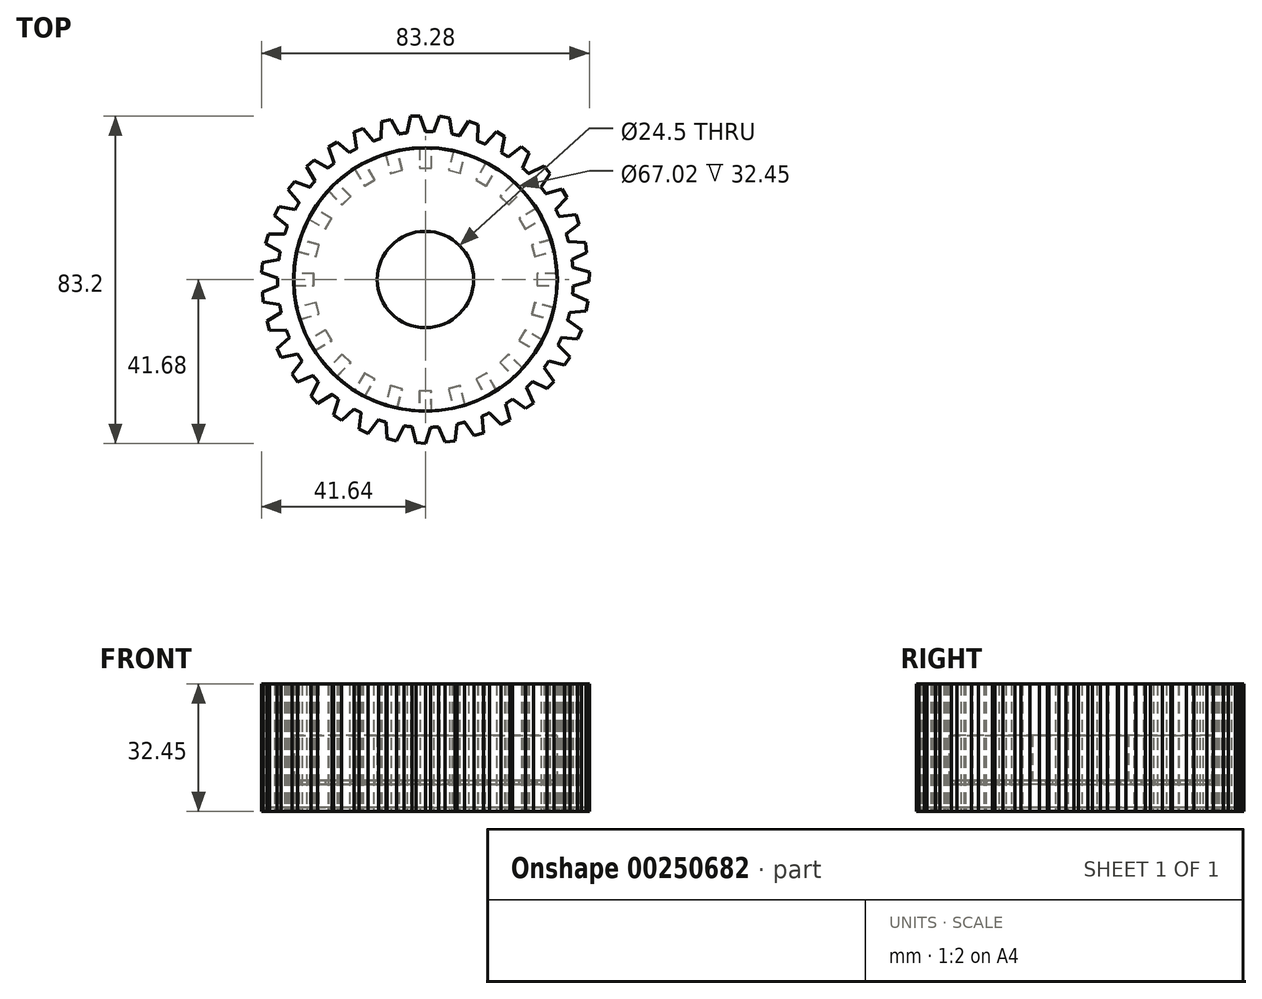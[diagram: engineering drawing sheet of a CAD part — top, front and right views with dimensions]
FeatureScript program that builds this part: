
annotation { "Feature Type Name" : "Feature", "Feature Type Description" : "" }
export const myFeature = defineFeature(function(context is Context, id is Id, definition is map)
    precondition{}
    {
        {
            var Q0;
            Q0=qCreatedBy(makeId("Top.planeOp"),FACE);
            var sketch = newSketch(context, id + "F0", { "sketchPlane" : qUnion([Q0])});
            skCircle(sketch, "E0", {"center": v(0, 0) * mm, "radius": 10.36 * mm});
            skCircle(sketch, "E1", {"center": v(0, 0) * mm, "radius": 33.51 * mm});
            skArc(sketch, "E2", {"start": v(-11.27, 35.85) * mm, "mid": v(-12.24, 35.53) * mm, "end": v(-13.2, 35.18) * mm});
            skLineSegment(sketch, "E3", {"start": v(-4.68, 37.29) * mm, "end": v(-3.82, 41.5) * mm});
            skLineSegment(sketch, "E4", {"start": v(-3.82, 41.5) * mm, "end": v(-1.33, 41.5) * mm});
            skLineSegment(sketch, "E5", {"start": v(-1.33, 41.5) * mm, "end": v(0, 37.58) * mm});
            skLineSegment(sketch, "E6.1.0", {"start": v(-11.27, 35.85) * mm, "end": v(-11.17, 40.16) * mm});
            skLineSegment(sketch, "E6.1.1", {"start": v(-11.17, 40.16) * mm, "end": v(-8.72, 40.6) * mm});
            skLineSegment(sketch, "E6.1.2", {"start": v(-8.72, 40.6) * mm, "end": v(-6.7, 36.97) * mm});
            skLineSegment(sketch, "E6.2.0", {"start": v(-17.49, 33.26) * mm, "end": v(-18.17, 37.52) * mm});
            skLineSegment(sketch, "E6.2.1", {"start": v(-18.17, 37.52) * mm, "end": v(-15.83, 38.4) * mm});
            skLineSegment(sketch, "E6.2.2", {"start": v(-15.83, 38.4) * mm, "end": v(-13.2, 35.18) * mm});
            skLineSegment(sketch, "E6.3.0", {"start": v(-23.14, 29.6) * mm, "end": v(-24.57, 33.67) * mm});
            skLineSegment(sketch, "E6.3.1", {"start": v(-24.57, 33.67) * mm, "end": v(-22.43, 34.95) * mm});
            skLineSegment(sketch, "E6.3.2", {"start": v(-22.43, 34.95) * mm, "end": v(-19.27, 32.26) * mm});
            skLineSegment(sketch, "E6.4.0", {"start": v(-28.06, 25) * mm, "end": v(-30.19, 28.74) * mm});
            skLineSegment(sketch, "E6.4.1", {"start": v(-30.19, 28.74) * mm, "end": v(-28.31, 30.38) * mm});
            skLineSegment(sketch, "E6.4.2", {"start": v(-28.31, 30.38) * mm, "end": v(-24.72, 28.3) * mm});
            skLineSegment(sketch, "E6.5.0", {"start": v(-32.07, 19.59) * mm, "end": v(-34.84, 22.89) * mm});
            skLineSegment(sketch, "E6.5.1", {"start": v(-34.84, 22.89) * mm, "end": v(-33.28, 24.84) * mm});
            skLineSegment(sketch, "E6.5.2", {"start": v(-33.28, 24.84) * mm, "end": v(-29.38, 23.43) * mm});
            skLineSegment(sketch, "E6.6.0", {"start": v(-35.05, 13.54) * mm, "end": v(-38.36, 16.3) * mm});
            skLineSegment(sketch, "E6.6.1", {"start": v(-38.36, 16.3) * mm, "end": v(-37.18, 18.5) * mm});
            skLineSegment(sketch, "E6.6.2", {"start": v(-37.18, 18.5) * mm, "end": v(-33.1, 17.8) * mm});
            skLineSegment(sketch, "E6.7.0", {"start": v(-36.9, 7.07) * mm, "end": v(-40.66, 9.19) * mm});
            skLineSegment(sketch, "E6.7.1", {"start": v(-40.66, 9.19) * mm, "end": v(-39.89, 11.56) * mm});
            skLineSegment(sketch, "E6.7.2", {"start": v(-39.89, 11.56) * mm, "end": v(-35.74, 11.61) * mm});
            skLineSegment(sketch, "E6.8.0", {"start": v(-37.58, 0.36) * mm, "end": v(-41.64, 1.78) * mm});
            skLineSegment(sketch, "E6.8.1", {"start": v(-41.64, 1.78) * mm, "end": v(-41.3, 4.25) * mm});
            skLineSegment(sketch, "E6.8.2", {"start": v(-41.3, 4.25) * mm, "end": v(-37.24, 5.04) * mm});
            skLineSegment(sketch, "E6.9.0", {"start": v(-37.04, -6.35) * mm, "end": v(-41.3, -5.68) * mm});
            skLineSegment(sketch, "E6.9.1", {"start": v(-41.3, -5.68) * mm, "end": v(-41.4, -3.2) * mm});
            skLineSegment(sketch, "E6.9.2", {"start": v(-41.4, -3.2) * mm, "end": v(-37.54, -1.69) * mm});
            skLineSegment(sketch, "E6.10.0", {"start": v(-35.3, -12.86) * mm, "end": v(-39.62, -12.97) * mm});
            skLineSegment(sketch, "E6.10.1", {"start": v(-39.62, -12.97) * mm, "end": v(-40.17, -10.53) * mm});
            skLineSegment(sketch, "E6.10.2", {"start": v(-40.17, -10.53) * mm, "end": v(-36.64, -8.36) * mm});
            skLineSegment(sketch, "E6.11.0", {"start": v(-32.44, -18.96) * mm, "end": v(-36.66, -19.83) * mm});
            skLineSegment(sketch, "E6.11.1", {"start": v(-36.66, -19.83) * mm, "end": v(-37.64, -17.54) * mm});
            skLineSegment(sketch, "E6.11.2", {"start": v(-37.64, -17.54) * mm, "end": v(-34.55, -14.77) * mm});
            skLineSegment(sketch, "E6.12.0", {"start": v(-28.54, -24.45) * mm, "end": v(-32.53, -26.06) * mm});
            skLineSegment(sketch, "E6.12.1", {"start": v(-32.53, -26.06) * mm, "end": v(-33.9, -23.98) * mm});
            skLineSegment(sketch, "E6.12.2", {"start": v(-33.9, -23.98) * mm, "end": v(-31.36, -20.7) * mm});
            skLineSegment(sketch, "E6.13.0", {"start": v(-23.71, -29.15) * mm, "end": v(-27.36, -31.45) * mm});
            skLineSegment(sketch, "E6.13.1", {"start": v(-27.36, -31.45) * mm, "end": v(-29.08, -29.64) * mm});
            skLineSegment(sketch, "E6.13.2", {"start": v(-29.08, -29.64) * mm, "end": v(-27.16, -25.97) * mm});
            skLineSegment(sketch, "E6.14.0", {"start": v(-18.13, -32.92) * mm, "end": v(-21.3, -35.83) * mm});
            skLineSegment(sketch, "E6.14.1", {"start": v(-21.3, -35.83) * mm, "end": v(-23.32, -34.36) * mm});
            skLineSegment(sketch, "E6.14.2", {"start": v(-23.32, -34.36) * mm, "end": v(-22.09, -30.4) * mm});
            skLineSegment(sketch, "E6.15.0", {"start": v(-11.96, -35.63) * mm, "end": v(-14.56, -39.06) * mm});
            skLineSegment(sketch, "E6.15.1", {"start": v(-14.56, -39.06) * mm, "end": v(-16.81, -37.97) * mm});
            skLineSegment(sketch, "E6.15.2", {"start": v(-16.81, -37.97) * mm, "end": v(-16.3, -33.86) * mm});
            skLineSegment(sketch, "E6.16.0", {"start": v(-5.4, -37.19) * mm, "end": v(-7.36, -41.03) * mm});
            skLineSegment(sketch, "E6.16.1", {"start": v(-7.36, -41.03) * mm, "end": v(-9.76, -40.36) * mm});
            skLineSegment(sketch, "E6.16.2", {"start": v(-9.76, -40.36) * mm, "end": v(-10, -36.22) * mm});
            skLineSegment(sketch, "E6.17.0", {"start": v(1.32, -37.56) * mm, "end": v(0.09, -41.68) * mm});
            skLineSegment(sketch, "E6.17.1", {"start": v(0.09, -41.68) * mm, "end": v(-2.4, -41.46) * mm});
            skLineSegment(sketch, "E6.17.2", {"start": v(-2.4, -41.46) * mm, "end": v(-3.37, -37.43) * mm});
            skLineSegment(sketch, "E6.18.0", {"start": v(8, -36.72) * mm, "end": v(7.53, -41) * mm});
            skLineSegment(sketch, "E6.18.1", {"start": v(7.53, -41) * mm, "end": v(5.04, -41.22) * mm});
            skLineSegment(sketch, "E6.18.2", {"start": v(5.04, -41.22) * mm, "end": v(3.37, -37.43) * mm});
            skLineSegment(sketch, "E6.19.0", {"start": v(14.43, -34.7) * mm, "end": v(14.73, -39) * mm});
            skLineSegment(sketch, "E6.19.1", {"start": v(14.73, -39) * mm, "end": v(12.32, -39.66) * mm});
            skLineSegment(sketch, "E6.19.2", {"start": v(12.32, -39.66) * mm, "end": v(10, -36.22) * mm});
            skLineSegment(sketch, "E6.20.0", {"start": v(20.4, -31.56) * mm, "end": v(21.46, -35.74) * mm});
            skLineSegment(sketch, "E6.20.1", {"start": v(21.46, -35.74) * mm, "end": v(19.2, -36.82) * mm});
            skLineSegment(sketch, "E6.20.2", {"start": v(19.2, -36.82) * mm, "end": v(16.3, -33.86) * mm});
            skLineSegment(sketch, "E6.21.0", {"start": v(25.7, -27.41) * mm, "end": v(27.5, -31.33) * mm});
            skLineSegment(sketch, "E6.21.1", {"start": v(27.5, -31.33) * mm, "end": v(25.47, -32.8) * mm});
            skLineSegment(sketch, "E6.21.2", {"start": v(25.47, -32.8) * mm, "end": v(22.09, -30.4) * mm});
            skLineSegment(sketch, "E6.22.0", {"start": v(30.19, -22.38) * mm, "end": v(32.64, -25.92) * mm});
            skLineSegment(sketch, "E6.22.1", {"start": v(32.64, -25.92) * mm, "end": v(30.92, -27.72) * mm});
            skLineSegment(sketch, "E6.22.2", {"start": v(30.92, -27.72) * mm, "end": v(27.16, -25.97) * mm});
            skLineSegment(sketch, "E6.23.0", {"start": v(33.7, -16.63) * mm, "end": v(36.75, -19.67) * mm});
            skLineSegment(sketch, "E6.23.1", {"start": v(36.75, -19.67) * mm, "end": v(35.37, -21.76) * mm});
            skLineSegment(sketch, "E6.23.2", {"start": v(35.37, -21.76) * mm, "end": v(31.36, -20.7) * mm});
            skLineSegment(sketch, "E6.24.0", {"start": v(36.13, -10.35) * mm, "end": v(39.67, -12.8) * mm});
            skLineSegment(sketch, "E6.24.1", {"start": v(39.67, -12.8) * mm, "end": v(38.69, -15.1) * mm});
            skLineSegment(sketch, "E6.24.2", {"start": v(38.69, -15.1) * mm, "end": v(34.55, -14.77) * mm});
            skLineSegment(sketch, "E6.25.0", {"start": v(37.4, -3.73) * mm, "end": v(41.32, -5.5) * mm});
            skLineSegment(sketch, "E6.25.1", {"start": v(41.32, -5.5) * mm, "end": v(40.76, -7.94) * mm});
            skLineSegment(sketch, "E6.25.2", {"start": v(40.76, -7.94) * mm, "end": v(36.64, -8.36) * mm});
            skLineSegment(sketch, "E6.26.0", {"start": v(37.46, 3) * mm, "end": v(41.64, 1.96) * mm});
            skLineSegment(sketch, "E6.26.1", {"start": v(41.64, 1.96) * mm, "end": v(41.53, -0.53) * mm});
            skLineSegment(sketch, "E6.26.2", {"start": v(41.53, -0.53) * mm, "end": v(37.54, -1.69) * mm});
            skLineSegment(sketch, "E6.27.0", {"start": v(36.32, 9.65) * mm, "end": v(40.62, 9.36) * mm});
            skLineSegment(sketch, "E6.27.1", {"start": v(40.62, 9.36) * mm, "end": v(40.95, 6.89) * mm});
            skLineSegment(sketch, "E6.27.2", {"start": v(40.95, 6.89) * mm, "end": v(37.24, 5.04) * mm});
            skLineSegment(sketch, "E6.28.0", {"start": v(34.01, 15.98) * mm, "end": v(38.3, 16.46) * mm});
            skLineSegment(sketch, "E6.28.1", {"start": v(38.3, 16.46) * mm, "end": v(39.06, 14.1) * mm});
            skLineSegment(sketch, "E6.28.2", {"start": v(39.06, 14.1) * mm, "end": v(35.74, 11.61) * mm});
            skLineSegment(sketch, "E6.29.0", {"start": v(30.61, 21.8) * mm, "end": v(34.74, 23.04) * mm});
            skLineSegment(sketch, "E6.29.1", {"start": v(34.74, 23.04) * mm, "end": v(35.92, 20.84) * mm});
            skLineSegment(sketch, "E6.29.2", {"start": v(35.92, 20.84) * mm, "end": v(33.1, 17.8) * mm});
            skLineSegment(sketch, "E6.30.0", {"start": v(26.23, 26.9) * mm, "end": v(30.07, 28.87) * mm});
            skLineSegment(sketch, "E6.30.1", {"start": v(30.07, 28.87) * mm, "end": v(31.62, 26.92) * mm});
            skLineSegment(sketch, "E6.30.2", {"start": v(31.62, 26.92) * mm, "end": v(29.38, 23.43) * mm});
            skLineSegment(sketch, "E6.31.0", {"start": v(21, 31.16) * mm, "end": v(24.43, 33.77) * mm});
            skLineSegment(sketch, "E6.31.1", {"start": v(24.43, 33.77) * mm, "end": v(26.3, 32.13) * mm});
            skLineSegment(sketch, "E6.31.2", {"start": v(26.3, 32.13) * mm, "end": v(24.72, 28.3) * mm});
            skLineSegment(sketch, "E6.32.0", {"start": v(15.1, 34.4) * mm, "end": v(18, 37.6) * mm});
            skLineSegment(sketch, "E6.32.1", {"start": v(18, 37.6) * mm, "end": v(20.15, 36.31) * mm});
            skLineSegment(sketch, "E6.32.2", {"start": v(20.15, 36.31) * mm, "end": v(19.27, 32.26) * mm});
            skLineSegment(sketch, "E6.33.0", {"start": v(8.72, 36.55) * mm, "end": v(11, 40.2) * mm});
            skLineSegment(sketch, "E6.33.1", {"start": v(11, 40.2) * mm, "end": v(13.34, 39.33) * mm});
            skLineSegment(sketch, "E6.33.2", {"start": v(13.34, 39.33) * mm, "end": v(13.2, 35.18) * mm});
            skLineSegment(sketch, "E6.34.0", {"start": v(2.05, 37.52) * mm, "end": v(3.65, 41.52) * mm});
            skLineSegment(sketch, "E6.34.1", {"start": v(3.65, 41.52) * mm, "end": v(6.1, 41.08) * mm});
            skLineSegment(sketch, "E6.34.2", {"start": v(6.1, 41.08) * mm, "end": v(6.7, 36.97) * mm});
            skArc(sketch, "E7.trimOffspring", {"start": v(-4.68, 37.29) * mm, "mid": v(-5.7, 37.14) * mm, "end": v(-6.7, 36.97) * mm});
            skArc(sketch, "E8.trimOffspring", {"start": v(2.05, 37.52) * mm, "mid": v(1.03, 37.56) * mm, "end": v(0, 37.58) * mm});
            skArc(sketch, "E9.trimOffspring", {"start": v(8.72, 36.55) * mm, "mid": v(7.72, 36.78) * mm, "end": v(6.7, 36.97) * mm});
            skArc(sketch, "E10.trimOffspring", {"start": v(15.1, 34.4) * mm, "mid": v(14.16, 34.8) * mm, "end": v(13.2, 35.18) * mm});
            skArc(sketch, "E11.trimOffspring", {"start": v(21, 31.16) * mm, "mid": v(20.15, 31.72) * mm, "end": v(19.27, 32.26) * mm});
            skArc(sketch, "E12.trimOffspring", {"start": v(26.23, 26.9) * mm, "mid": v(25.49, 27.61) * mm, "end": v(24.72, 28.3) * mm});
            skArc(sketch, "E13.trimOffspring", {"start": v(30.61, 21.8) * mm, "mid": v(30, 22.62) * mm, "end": v(29.38, 23.43) * mm});
            skArc(sketch, "E14.trimOffspring", {"start": v(34.01, 15.98) * mm, "mid": v(33.57, 16.9) * mm, "end": v(33.1, 17.8) * mm});
            skArc(sketch, "E15.trimOffspring", {"start": v(36.32, 9.65) * mm, "mid": v(36.04, 10.63) * mm, "end": v(35.74, 11.61) * mm});
            skArc(sketch, "E16.trimOffspring", {"start": v(37.46, 3) * mm, "mid": v(37.36, 4.03) * mm, "end": v(37.24, 5.04) * mm});
            skArc(sketch, "E17.trimOffspring", {"start": v(37.4, -3.73) * mm, "mid": v(37.48, -2.7) * mm, "end": v(37.54, -1.69) * mm});
            skArc(sketch, "E18.trimOffspring", {"start": v(36.13, -10.35) * mm, "mid": v(36.4, -9.36) * mm, "end": v(36.64, -8.36) * mm});
            skArc(sketch, "E19.trimOffspring", {"start": v(33.7, -16.63) * mm, "mid": v(34.14, -15.7) * mm, "end": v(34.55, -14.77) * mm});
            skArc(sketch, "E20.trimOffspring", {"start": v(30.19, -22.38) * mm, "mid": v(30.79, -21.55) * mm, "end": v(31.36, -20.7) * mm});
            skArc(sketch, "E21.trimOffspring", {"start": v(25.7, -27.41) * mm, "mid": v(26.44, -26.7) * mm, "end": v(27.16, -25.97) * mm});
            skArc(sketch, "E22.trimOffspring", {"start": v(20.4, -31.56) * mm, "mid": v(21.25, -31) * mm, "end": v(22.09, -30.4) * mm});
            skArc(sketch, "E23.trimOffspring", {"start": v(14.43, -34.7) * mm, "mid": v(15.37, -34.29) * mm, "end": v(16.3, -33.86) * mm});
            skArc(sketch, "E24.trimOffspring", {"start": v(8, -36.72) * mm, "mid": v(9, -36.48) * mm, "end": v(10, -36.22) * mm});
            skArc(sketch, "E25.trimOffspring", {"start": v(1.32, -37.56) * mm, "mid": v(2.35, -37.5) * mm, "end": v(3.37, -37.43) * mm});
            skArc(sketch, "E26.trimOffspring", {"start": v(-5.4, -37.19) * mm, "mid": v(-4.39, -37.32) * mm, "end": v(-3.37, -37.43) * mm});
            skArc(sketch, "E27.trimOffspring", {"start": v(-11.96, -35.63) * mm, "mid": v(-10.98, -35.94) * mm, "end": v(-10, -36.22) * mm});
            skArc(sketch, "E28.trimOffspring", {"start": v(-18.13, -32.92) * mm, "mid": v(-17.22, -33.4) * mm, "end": v(-16.3, -33.86) * mm});
            skArc(sketch, "E29.trimOffspring", {"start": v(-23.71, -29.15) * mm, "mid": v(-22.9, -29.79) * mm, "end": v(-22.09, -30.4) * mm});
            skArc(sketch, "E30.trimOffspring", {"start": v(-28.54, -24.45) * mm, "mid": v(-27.86, -25.22) * mm, "end": v(-27.16, -25.97) * mm});
            skArc(sketch, "E31.trimOffspring", {"start": v(-32.44, -18.96) * mm, "mid": v(-31.92, -19.84) * mm, "end": v(-31.36, -20.7) * mm});
            skArc(sketch, "E32.trimOffspring", {"start": v(-35.3, -12.86) * mm, "mid": v(-34.94, -13.82) * mm, "end": v(-34.55, -14.77) * mm});
            skArc(sketch, "E33.trimOffspring", {"start": v(-37.04, -6.35) * mm, "mid": v(-36.85, -7.36) * mm, "end": v(-36.64, -8.36) * mm});
            skArc(sketch, "E34.trimOffspring", {"start": v(-37.58, 0.36) * mm, "mid": v(-37.57, -0.66) * mm, "end": v(-37.54, -1.69) * mm});
            skArc(sketch, "E35.trimOffspring", {"start": v(-36.9, 7.07) * mm, "mid": v(-37.09, 6.06) * mm, "end": v(-37.24, 5.04) * mm});
            skArc(sketch, "E36.trimOffspring", {"start": v(-35.05, 13.54) * mm, "mid": v(-35.4, 12.58) * mm, "end": v(-35.74, 11.61) * mm});
            skArc(sketch, "E37.trimOffspring", {"start": v(-32.07, 19.59) * mm, "mid": v(-32.6, 18.7) * mm, "end": v(-33.1, 17.8) * mm});
            skArc(sketch, "E38.trimOffspring", {"start": v(-28.06, 25) * mm, "mid": v(-28.73, 24.22) * mm, "end": v(-29.38, 23.43) * mm});
            skArc(sketch, "E39.trimOffspring", {"start": v(-23.14, 29.6) * mm, "mid": v(-23.94, 28.96) * mm, "end": v(-24.72, 28.3) * mm});
            skArc(sketch, "E40.trimOffspring", {"start": v(-17.49, 33.26) * mm, "mid": v(-18.39, 32.77) * mm, "end": v(-19.27, 32.26) * mm});
            skSolve(sketch);
        }
        {
            var Q0;
            Q0 = qSketchRegion(id + "F0", true);
            extrude(context, id + "F1", {"entities" : qUnion([Q0]), "endBound" : BoundingType.SYMMETRIC, "depth" : 26.2 * mm});
        }
        {
            var Q0;
            Q0=qCreatedBy(makeId("Top.planeOp"),FACE);
            var sketch = newSketch(context, id + "F2", { "sketchPlane" : qUnion([Q0])});
            skCircle(sketch, "E41", {"center": v(0, 0) * mm, "radius": 33.42 * mm});
            skCircle(sketch, "E42", {"center": v(0, 0) * mm, "radius": 12.25 * mm});
            skSolve(sketch);
        }
        {
            var Q0;
            Q0 = qSketchRegion(id + "F2", true);
            var Q1;
            Q1=makeQuery(id+"F1.opExtrude","CAP_FACE",FACE,{"disambiguationData":[OSD([sQuery(id+"F0.wireOp",EDGE,"E1"),sQuery(id+"F0.wireOp",EDGE,"E2"),sQuery(id+"F0.wireOp",EDGE,"E3"),sQuery(id+"F0.wireOp",EDGE,"E4"),sQuery(id+"F0.wireOp",EDGE,"E5"),sQuery(id+"F0.wireOp",EDGE,"E6.1.0"),sQuery(id+"F0.wireOp",EDGE,"E6.1.1"),sQuery(id+"F0.wireOp",EDGE,"E6.1.2"),sQuery(id+"F0.wireOp",EDGE,"E6.2.0"),sQuery(id+"F0.wireOp",EDGE,"E6.2.1"),sQuery(id+"F0.wireOp",EDGE,"E6.2.2"),sQuery(id+"F0.wireOp",EDGE,"E6.3.0"),sQuery(id+"F0.wireOp",EDGE,"E6.3.1"),sQuery(id+"F0.wireOp",EDGE,"E6.3.2"),sQuery(id+"F0.wireOp",EDGE,"E6.4.0"),sQuery(id+"F0.wireOp",EDGE,"E6.4.1"),sQuery(id+"F0.wireOp",EDGE,"E6.4.2"),sQuery(id+"F0.wireOp",EDGE,"E6.5.0"),sQuery(id+"F0.wireOp",EDGE,"E6.5.1"),sQuery(id+"F0.wireOp",EDGE,"E6.5.2"),sQuery(id+"F0.wireOp",EDGE,"E6.6.0"),sQuery(id+"F0.wireOp",EDGE,"E6.6.1"),sQuery(id+"F0.wireOp",EDGE,"E6.6.2"),sQuery(id+"F0.wireOp",EDGE,"E6.7.0"),sQuery(id+"F0.wireOp",EDGE,"E6.7.1"),sQuery(id+"F0.wireOp",EDGE,"E6.7.2"),sQuery(id+"F0.wireOp",EDGE,"E6.8.0"),sQuery(id+"F0.wireOp",EDGE,"E6.8.1"),sQuery(id+"F0.wireOp",EDGE,"E6.8.2"),sQuery(id+"F0.wireOp",EDGE,"E6.9.0"),sQuery(id+"F0.wireOp",EDGE,"E6.9.1"),sQuery(id+"F0.wireOp",EDGE,"E6.9.2"),sQuery(id+"F0.wireOp",EDGE,"E6.10.0"),sQuery(id+"F0.wireOp",EDGE,"E6.10.1"),sQuery(id+"F0.wireOp",EDGE,"E6.10.2"),sQuery(id+"F0.wireOp",EDGE,"E6.11.0"),sQuery(id+"F0.wireOp",EDGE,"E6.11.1"),sQuery(id+"F0.wireOp",EDGE,"E6.11.2"),sQuery(id+"F0.wireOp",EDGE,"E6.12.0"),sQuery(id+"F0.wireOp",EDGE,"E6.12.1"),sQuery(id+"F0.wireOp",EDGE,"E6.12.2"),sQuery(id+"F0.wireOp",EDGE,"E6.13.0"),sQuery(id+"F0.wireOp",EDGE,"E6.13.1"),sQuery(id+"F0.wireOp",EDGE,"E6.13.2"),sQuery(id+"F0.wireOp",EDGE,"E6.14.0"),sQuery(id+"F0.wireOp",EDGE,"E6.14.1"),sQuery(id+"F0.wireOp",EDGE,"E6.14.2"),sQuery(id+"F0.wireOp",EDGE,"E6.15.0"),sQuery(id+"F0.wireOp",EDGE,"E6.15.1"),sQuery(id+"F0.wireOp",EDGE,"E6.15.2"),sQuery(id+"F0.wireOp",EDGE,"E6.16.0"),sQuery(id+"F0.wireOp",EDGE,"E6.16.1"),sQuery(id+"F0.wireOp",EDGE,"E6.16.2"),sQuery(id+"F0.wireOp",EDGE,"E6.17.0"),sQuery(id+"F0.wireOp",EDGE,"E6.17.1"),sQuery(id+"F0.wireOp",EDGE,"E6.17.2"),sQuery(id+"F0.wireOp",EDGE,"E6.18.0"),sQuery(id+"F0.wireOp",EDGE,"E6.18.1"),sQuery(id+"F0.wireOp",EDGE,"E6.18.2"),sQuery(id+"F0.wireOp",EDGE,"E6.19.0"),sQuery(id+"F0.wireOp",EDGE,"E6.19.1"),sQuery(id+"F0.wireOp",EDGE,"E6.19.2"),sQuery(id+"F0.wireOp",EDGE,"E6.20.0"),sQuery(id+"F0.wireOp",EDGE,"E6.20.1"),sQuery(id+"F0.wireOp",EDGE,"E6.20.2"),sQuery(id+"F0.wireOp",EDGE,"E6.21.0"),sQuery(id+"F0.wireOp",EDGE,"E6.21.1"),sQuery(id+"F0.wireOp",EDGE,"E6.21.2"),sQuery(id+"F0.wireOp",EDGE,"E6.22.0"),sQuery(id+"F0.wireOp",EDGE,"E6.22.1"),sQuery(id+"F0.wireOp",EDGE,"E6.22.2"),sQuery(id+"F0.wireOp",EDGE,"E6.23.0"),sQuery(id+"F0.wireOp",EDGE,"E6.23.1"),sQuery(id+"F0.wireOp",EDGE,"E6.23.2"),sQuery(id+"F0.wireOp",EDGE,"E6.24.0"),sQuery(id+"F0.wireOp",EDGE,"E6.24.1"),sQuery(id+"F0.wireOp",EDGE,"E6.24.2"),sQuery(id+"F0.wireOp",EDGE,"E6.25.0"),sQuery(id+"F0.wireOp",EDGE,"E6.25.1"),sQuery(id+"F0.wireOp",EDGE,"E6.25.2"),sQuery(id+"F0.wireOp",EDGE,"E6.26.0"),sQuery(id+"F0.wireOp",EDGE,"E6.26.1"),sQuery(id+"F0.wireOp",EDGE,"E6.26.2"),sQuery(id+"F0.wireOp",EDGE,"E6.27.0"),sQuery(id+"F0.wireOp",EDGE,"E6.27.1"),sQuery(id+"F0.wireOp",EDGE,"E6.27.2"),sQuery(id+"F0.wireOp",EDGE,"E6.28.0"),sQuery(id+"F0.wireOp",EDGE,"E6.28.1"),sQuery(id+"F0.wireOp",EDGE,"E6.28.2"),sQuery(id+"F0.wireOp",EDGE,"E6.29.0"),sQuery(id+"F0.wireOp",EDGE,"E6.29.1"),sQuery(id+"F0.wireOp",EDGE,"E6.29.2"),sQuery(id+"F0.wireOp",EDGE,"E6.30.0"),sQuery(id+"F0.wireOp",EDGE,"E6.30.1"),sQuery(id+"F0.wireOp",EDGE,"E6.30.2"),sQuery(id+"F0.wireOp",EDGE,"E6.31.0"),sQuery(id+"F0.wireOp",EDGE,"E6.31.1"),sQuery(id+"F0.wireOp",EDGE,"E6.31.2"),sQuery(id+"F0.wireOp",EDGE,"E6.32.0"),sQuery(id+"F0.wireOp",EDGE,"E6.32.1"),sQuery(id+"F0.wireOp",EDGE,"E6.32.2"),sQuery(id+"F0.wireOp",EDGE,"E6.33.0"),sQuery(id+"F0.wireOp",EDGE,"E6.33.1"),sQuery(id+"F0.wireOp",EDGE,"E6.33.2"),sQuery(id+"F0.wireOp",EDGE,"E6.34.0"),sQuery(id+"F0.wireOp",EDGE,"E6.34.1"),sQuery(id+"F0.wireOp",EDGE,"E6.34.2"),sQuery(id+"F0.wireOp",EDGE,"E7.trimOffspring"),sQuery(id+"F0.wireOp",EDGE,"E8.trimOffspring"),sQuery(id+"F0.wireOp",EDGE,"E9.trimOffspring"),sQuery(id+"F0.wireOp",EDGE,"E10.trimOffspring"),sQuery(id+"F0.wireOp",EDGE,"E11.trimOffspring"),sQuery(id+"F0.wireOp",EDGE,"E12.trimOffspring"),sQuery(id+"F0.wireOp",EDGE,"E13.trimOffspring"),sQuery(id+"F0.wireOp",EDGE,"E14.trimOffspring"),sQuery(id+"F0.wireOp",EDGE,"E15.trimOffspring"),sQuery(id+"F0.wireOp",EDGE,"E16.trimOffspring"),sQuery(id+"F0.wireOp",EDGE,"E17.trimOffspring"),sQuery(id+"F0.wireOp",EDGE,"E18.trimOffspring"),sQuery(id+"F0.wireOp",EDGE,"E19.trimOffspring"),sQuery(id+"F0.wireOp",EDGE,"E20.trimOffspring"),sQuery(id+"F0.wireOp",EDGE,"E21.trimOffspring"),sQuery(id+"F0.wireOp",EDGE,"E22.trimOffspring"),sQuery(id+"F0.wireOp",EDGE,"E23.trimOffspring"),sQuery(id+"F0.wireOp",EDGE,"E24.trimOffspring"),sQuery(id+"F0.wireOp",EDGE,"E25.trimOffspring"),sQuery(id+"F0.wireOp",EDGE,"E26.trimOffspring"),sQuery(id+"F0.wireOp",EDGE,"E27.trimOffspring"),sQuery(id+"F0.wireOp",EDGE,"E28.trimOffspring"),sQuery(id+"F0.wireOp",EDGE,"E29.trimOffspring"),sQuery(id+"F0.wireOp",EDGE,"E30.trimOffspring"),sQuery(id+"F0.wireOp",EDGE,"E31.trimOffspring"),sQuery(id+"F0.wireOp",EDGE,"E32.trimOffspring"),sQuery(id+"F0.wireOp",EDGE,"E33.trimOffspring"),sQuery(id+"F0.wireOp",EDGE,"E34.trimOffspring"),sQuery(id+"F0.wireOp",EDGE,"E35.trimOffspring"),sQuery(id+"F0.wireOp",EDGE,"E36.trimOffspring"),sQuery(id+"F0.wireOp",EDGE,"E37.trimOffspring"),sQuery(id+"F0.wireOp",EDGE,"E38.trimOffspring"),sQuery(id+"F0.wireOp",EDGE,"E39.trimOffspring"),sQuery(id+"F0.wireOp",EDGE,"E40.trimOffspring")])],"isStart":false});
            extrude(context, id + "F3", {"entities" : qUnion([Q0, Q1]), "operationType" : NewBodyOperationType.ADD, "endBound" : BoundingType.SYMMETRIC, "depth" : 12.5 * mm});
        }
        {
            var Q0;
            Q0=makeQuery(id+"F3.opExtrude","CAP_FACE",FACE,{"disambiguationData":[OSD([sQuery(id+"F2.wireOp",EDGE,"E41"),sQuery(id+"F2.wireOp",EDGE,"E42")])],"isStart":true});
            var sketch = newSketch(context, id + "F4", { "sketchPlane" : qUnion([Q0])});
            skLineSegment(sketch, "E43", {"start": v(0, 0) * mm, "end": v(0, 33.42) * mm, "construction": true});
            skLineSegment(sketch, "E44.bottom", {"start": v(-1.51, 28.38) * mm, "end": v(1.49, 28.38) * mm});
            skLineSegment(sketch, "E44.left", {"start": v(-1.51, 28.38) * mm, "end": v(-1.5, 33.38) * mm});
            skLineSegment(sketch, "E44.right", {"start": v(1.49, 28.38) * mm, "end": v(1.5, 33.38) * mm});
            skPoint(sketch, "E44.middle", {"position": v(0, 33.42) * mm});
            skCircle(sketch, "E45.0", {"center": v(0, 0) * mm, "radius": 33.42 * mm});
            skPoint(sketch, "E44.top.start.orphan", {"position": v(-1.49, 38.45) * mm});
            skPoint(sketch, "E46.orphan", {"position": v(1.51, 38.45) * mm});
            skLineSegment(sketch, "E47.1.0", {"start": v(-5.91, 27.8) * mm, "end": v(-7.2, 32.63) * mm});
            skLineSegment(sketch, "E47.1.1", {"start": v(-8.8, 27.02) * mm, "end": v(-5.91, 27.8) * mm});
            skLineSegment(sketch, "E47.1.2", {"start": v(-8.8, 27.02) * mm, "end": v(-10.09, 31.86) * mm});
            skLineSegment(sketch, "E47.2.0", {"start": v(-12.9, 25.32) * mm, "end": v(-15.4, 29.66) * mm});
            skLineSegment(sketch, "E47.2.1", {"start": v(-15.5, 23.82) * mm, "end": v(-12.9, 25.32) * mm});
            skLineSegment(sketch, "E47.2.2", {"start": v(-15.5, 23.82) * mm, "end": v(-17.99, 28.16) * mm});
            skLineSegment(sketch, "E47.3.0", {"start": v(-19.02, 21.12) * mm, "end": v(-22.54, 24.66) * mm});
            skLineSegment(sketch, "E47.3.1", {"start": v(-21.14, 19) * mm, "end": v(-19.02, 21.12) * mm});
            skLineSegment(sketch, "E47.3.2", {"start": v(-21.14, 19) * mm, "end": v(-24.67, 22.54) * mm});
            skLineSegment(sketch, "E47.4.0", {"start": v(-23.84, 15.48) * mm, "end": v(-28.16, 17.99) * mm});
            skLineSegment(sketch, "E47.4.1", {"start": v(-25.34, 12.88) * mm, "end": v(-23.84, 15.48) * mm});
            skLineSegment(sketch, "E47.4.2", {"start": v(-25.34, 12.88) * mm, "end": v(-29.66, 15.4) * mm});
            skLineSegment(sketch, "E47.5.0", {"start": v(-27.03, 8.78) * mm, "end": v(-31.86, 10.09) * mm});
            skLineSegment(sketch, "E47.5.1", {"start": v(-27.8, 5.88) * mm, "end": v(-27.03, 8.78) * mm});
            skLineSegment(sketch, "E47.5.2", {"start": v(-27.8, 5.88) * mm, "end": v(-32.63, 7.2) * mm});
            skLineSegment(sketch, "E47.6.0", {"start": v(-28.38, 1.49) * mm, "end": v(-33.38, 1.5) * mm});
            skLineSegment(sketch, "E47.6.1", {"start": v(-28.38, -1.51) * mm, "end": v(-28.38, 1.49) * mm});
            skLineSegment(sketch, "E47.6.2", {"start": v(-28.38, -1.51) * mm, "end": v(-33.38, -1.5) * mm});
            skLineSegment(sketch, "E47.7.0", {"start": v(-27.8, -5.91) * mm, "end": v(-32.63, -7.2) * mm});
            skLineSegment(sketch, "E47.7.1", {"start": v(-27.02, -8.8) * mm, "end": v(-27.8, -5.91) * mm});
            skLineSegment(sketch, "E47.7.2", {"start": v(-27.02, -8.8) * mm, "end": v(-31.86, -10.09) * mm});
            skLineSegment(sketch, "E47.8.0", {"start": v(-25.32, -12.9) * mm, "end": v(-29.66, -15.4) * mm});
            skLineSegment(sketch, "E47.8.1", {"start": v(-23.82, -15.5) * mm, "end": v(-25.32, -12.9) * mm});
            skLineSegment(sketch, "E47.8.2", {"start": v(-23.82, -15.5) * mm, "end": v(-28.16, -17.99) * mm});
            skLineSegment(sketch, "E47.9.0", {"start": v(-21.12, -19.02) * mm, "end": v(-24.66, -22.54) * mm});
            skLineSegment(sketch, "E47.9.1", {"start": v(-19, -21.14) * mm, "end": v(-21.12, -19.02) * mm});
            skLineSegment(sketch, "E47.9.2", {"start": v(-19, -21.14) * mm, "end": v(-22.54, -24.67) * mm});
            skLineSegment(sketch, "E47.10.0", {"start": v(-15.48, -23.84) * mm, "end": v(-17.99, -28.16) * mm});
            skLineSegment(sketch, "E47.10.1", {"start": v(-12.88, -25.34) * mm, "end": v(-15.48, -23.84) * mm});
            skLineSegment(sketch, "E47.10.2", {"start": v(-12.88, -25.34) * mm, "end": v(-15.4, -29.66) * mm});
            skLineSegment(sketch, "E47.11.0", {"start": v(-8.78, -27.03) * mm, "end": v(-10.09, -31.86) * mm});
            skLineSegment(sketch, "E47.11.1", {"start": v(-5.88, -27.8) * mm, "end": v(-8.78, -27.03) * mm});
            skLineSegment(sketch, "E47.11.2", {"start": v(-5.88, -27.8) * mm, "end": v(-7.2, -32.63) * mm});
            skLineSegment(sketch, "E47.12.0", {"start": v(-1.49, -28.38) * mm, "end": v(-1.5, -33.38) * mm});
            skLineSegment(sketch, "E47.12.1", {"start": v(1.51, -28.38) * mm, "end": v(-1.49, -28.38) * mm});
            skLineSegment(sketch, "E47.12.2", {"start": v(1.51, -28.38) * mm, "end": v(1.5, -33.38) * mm});
            skLineSegment(sketch, "E47.13.0", {"start": v(5.91, -27.8) * mm, "end": v(7.2, -32.63) * mm});
            skLineSegment(sketch, "E47.13.1", {"start": v(8.8, -27.02) * mm, "end": v(5.91, -27.8) * mm});
            skLineSegment(sketch, "E47.13.2", {"start": v(8.8, -27.02) * mm, "end": v(10.09, -31.86) * mm});
            skLineSegment(sketch, "E47.14.0", {"start": v(12.9, -25.32) * mm, "end": v(15.4, -29.66) * mm});
            skLineSegment(sketch, "E47.14.1", {"start": v(15.5, -23.82) * mm, "end": v(12.9, -25.32) * mm});
            skLineSegment(sketch, "E47.14.2", {"start": v(15.5, -23.82) * mm, "end": v(17.99, -28.16) * mm});
            skLineSegment(sketch, "E47.15.0", {"start": v(19.02, -21.12) * mm, "end": v(22.54, -24.66) * mm});
            skLineSegment(sketch, "E47.15.1", {"start": v(21.14, -19) * mm, "end": v(19.02, -21.12) * mm});
            skLineSegment(sketch, "E47.15.2", {"start": v(21.14, -19) * mm, "end": v(24.67, -22.54) * mm});
            skLineSegment(sketch, "E47.16.0", {"start": v(23.84, -15.48) * mm, "end": v(28.16, -17.99) * mm});
            skLineSegment(sketch, "E47.16.1", {"start": v(25.34, -12.88) * mm, "end": v(23.84, -15.48) * mm});
            skLineSegment(sketch, "E47.16.2", {"start": v(25.34, -12.88) * mm, "end": v(29.66, -15.4) * mm});
            skLineSegment(sketch, "E47.17.0", {"start": v(27.03, -8.78) * mm, "end": v(31.86, -10.09) * mm});
            skLineSegment(sketch, "E47.17.1", {"start": v(27.8, -5.88) * mm, "end": v(27.03, -8.78) * mm});
            skLineSegment(sketch, "E47.17.2", {"start": v(27.8, -5.88) * mm, "end": v(32.63, -7.2) * mm});
            skLineSegment(sketch, "E47.18.0", {"start": v(28.38, -1.49) * mm, "end": v(33.38, -1.5) * mm});
            skLineSegment(sketch, "E47.18.1", {"start": v(28.38, 1.51) * mm, "end": v(28.38, -1.49) * mm});
            skLineSegment(sketch, "E47.18.2", {"start": v(28.38, 1.51) * mm, "end": v(33.38, 1.5) * mm});
            skLineSegment(sketch, "E47.19.0", {"start": v(27.8, 5.91) * mm, "end": v(32.63, 7.2) * mm});
            skLineSegment(sketch, "E47.19.1", {"start": v(27.02, 8.8) * mm, "end": v(27.8, 5.91) * mm});
            skLineSegment(sketch, "E47.19.2", {"start": v(27.02, 8.8) * mm, "end": v(31.86, 10.09) * mm});
            skLineSegment(sketch, "E47.20.0", {"start": v(25.32, 12.9) * mm, "end": v(29.66, 15.4) * mm});
            skLineSegment(sketch, "E47.20.1", {"start": v(23.82, 15.5) * mm, "end": v(25.32, 12.9) * mm});
            skLineSegment(sketch, "E47.20.2", {"start": v(23.82, 15.5) * mm, "end": v(28.16, 17.99) * mm});
            skLineSegment(sketch, "E47.21.0", {"start": v(21.12, 19.02) * mm, "end": v(24.66, 22.54) * mm});
            skLineSegment(sketch, "E47.21.1", {"start": v(19, 21.14) * mm, "end": v(21.12, 19.02) * mm});
            skLineSegment(sketch, "E47.21.2", {"start": v(19, 21.14) * mm, "end": v(22.54, 24.67) * mm});
            skLineSegment(sketch, "E47.22.0", {"start": v(15.48, 23.84) * mm, "end": v(17.99, 28.16) * mm});
            skLineSegment(sketch, "E47.22.1", {"start": v(12.88, 25.34) * mm, "end": v(15.48, 23.84) * mm});
            skLineSegment(sketch, "E47.22.2", {"start": v(12.88, 25.34) * mm, "end": v(15.4, 29.66) * mm});
            skLineSegment(sketch, "E47.23.0", {"start": v(8.78, 27.03) * mm, "end": v(10.09, 31.86) * mm});
            skLineSegment(sketch, "E47.23.1", {"start": v(5.88, 27.8) * mm, "end": v(8.78, 27.03) * mm});
            skLineSegment(sketch, "E47.23.2", {"start": v(5.88, 27.8) * mm, "end": v(7.2, 32.63) * mm});
            skSolve(sketch);
        }
        {
            var Q0;
            Q0=makeQuery(id+"F4.imprint","IMPRINT",FACE,{"disambiguationData":[TD([[makeQuery(id+"F4.imprint","IMPRINT",EDGE,{"derivedFrom":makeQuery(id+"F3.opExtrude","CAP_EDGE",EDGE,{"disambiguationData":[OSD([sQuery(id+"F2.wireOp",EDGE,"E42")])],"isStart":true})}),-1.0]])]});
            var Q1;
            Q1=makeQuery(id+"F4.imprint","IMPRINT",FACE,{"disambiguationData":[TD([[makeQuery(id+"F4.imprint","IMPRINT",EDGE,{"derivedFrom":sQuery(id+"F4.wireOp",EDGE,"E44.bottom")}),-1.0]])]});
            var Q2;
            Q2=makeQuery(id+"F1.opExtrude","CAP_FACE",FACE,{"disambiguationData":[OSD([sQuery(id+"F0.wireOp",EDGE,"E1"),sQuery(id+"F0.wireOp",EDGE,"E2"),sQuery(id+"F0.wireOp",EDGE,"E3"),sQuery(id+"F0.wireOp",EDGE,"E4"),sQuery(id+"F0.wireOp",EDGE,"E5"),sQuery(id+"F0.wireOp",EDGE,"E6.1.0"),sQuery(id+"F0.wireOp",EDGE,"E6.1.1"),sQuery(id+"F0.wireOp",EDGE,"E6.1.2"),sQuery(id+"F0.wireOp",EDGE,"E6.2.0"),sQuery(id+"F0.wireOp",EDGE,"E6.2.1"),sQuery(id+"F0.wireOp",EDGE,"E6.2.2"),sQuery(id+"F0.wireOp",EDGE,"E6.3.0"),sQuery(id+"F0.wireOp",EDGE,"E6.3.1"),sQuery(id+"F0.wireOp",EDGE,"E6.3.2"),sQuery(id+"F0.wireOp",EDGE,"E6.4.0"),sQuery(id+"F0.wireOp",EDGE,"E6.4.1"),sQuery(id+"F0.wireOp",EDGE,"E6.4.2"),sQuery(id+"F0.wireOp",EDGE,"E6.5.0"),sQuery(id+"F0.wireOp",EDGE,"E6.5.1"),sQuery(id+"F0.wireOp",EDGE,"E6.5.2"),sQuery(id+"F0.wireOp",EDGE,"E6.6.0"),sQuery(id+"F0.wireOp",EDGE,"E6.6.1"),sQuery(id+"F0.wireOp",EDGE,"E6.6.2"),sQuery(id+"F0.wireOp",EDGE,"E6.7.0"),sQuery(id+"F0.wireOp",EDGE,"E6.7.1"),sQuery(id+"F0.wireOp",EDGE,"E6.7.2"),sQuery(id+"F0.wireOp",EDGE,"E6.8.0"),sQuery(id+"F0.wireOp",EDGE,"E6.8.1"),sQuery(id+"F0.wireOp",EDGE,"E6.8.2"),sQuery(id+"F0.wireOp",EDGE,"E6.9.0"),sQuery(id+"F0.wireOp",EDGE,"E6.9.1"),sQuery(id+"F0.wireOp",EDGE,"E6.9.2"),sQuery(id+"F0.wireOp",EDGE,"E6.10.0"),sQuery(id+"F0.wireOp",EDGE,"E6.10.1"),sQuery(id+"F0.wireOp",EDGE,"E6.10.2"),sQuery(id+"F0.wireOp",EDGE,"E6.11.0"),sQuery(id+"F0.wireOp",EDGE,"E6.11.1"),sQuery(id+"F0.wireOp",EDGE,"E6.11.2"),sQuery(id+"F0.wireOp",EDGE,"E6.12.0"),sQuery(id+"F0.wireOp",EDGE,"E6.12.1"),sQuery(id+"F0.wireOp",EDGE,"E6.12.2"),sQuery(id+"F0.wireOp",EDGE,"E6.13.0"),sQuery(id+"F0.wireOp",EDGE,"E6.13.1"),sQuery(id+"F0.wireOp",EDGE,"E6.13.2"),sQuery(id+"F0.wireOp",EDGE,"E6.14.0"),sQuery(id+"F0.wireOp",EDGE,"E6.14.1"),sQuery(id+"F0.wireOp",EDGE,"E6.14.2"),sQuery(id+"F0.wireOp",EDGE,"E6.15.0"),sQuery(id+"F0.wireOp",EDGE,"E6.15.1"),sQuery(id+"F0.wireOp",EDGE,"E6.15.2"),sQuery(id+"F0.wireOp",EDGE,"E6.16.0"),sQuery(id+"F0.wireOp",EDGE,"E6.16.1"),sQuery(id+"F0.wireOp",EDGE,"E6.16.2"),sQuery(id+"F0.wireOp",EDGE,"E6.17.0"),sQuery(id+"F0.wireOp",EDGE,"E6.17.1"),sQuery(id+"F0.wireOp",EDGE,"E6.17.2"),sQuery(id+"F0.wireOp",EDGE,"E6.18.0"),sQuery(id+"F0.wireOp",EDGE,"E6.18.1"),sQuery(id+"F0.wireOp",EDGE,"E6.18.2"),sQuery(id+"F0.wireOp",EDGE,"E6.19.0"),sQuery(id+"F0.wireOp",EDGE,"E6.19.1"),sQuery(id+"F0.wireOp",EDGE,"E6.19.2"),sQuery(id+"F0.wireOp",EDGE,"E6.20.0"),sQuery(id+"F0.wireOp",EDGE,"E6.20.1"),sQuery(id+"F0.wireOp",EDGE,"E6.20.2"),sQuery(id+"F0.wireOp",EDGE,"E6.21.0"),sQuery(id+"F0.wireOp",EDGE,"E6.21.1"),sQuery(id+"F0.wireOp",EDGE,"E6.21.2"),sQuery(id+"F0.wireOp",EDGE,"E6.22.0"),sQuery(id+"F0.wireOp",EDGE,"E6.22.1"),sQuery(id+"F0.wireOp",EDGE,"E6.22.2"),sQuery(id+"F0.wireOp",EDGE,"E6.23.0"),sQuery(id+"F0.wireOp",EDGE,"E6.23.1"),sQuery(id+"F0.wireOp",EDGE,"E6.23.2"),sQuery(id+"F0.wireOp",EDGE,"E6.24.0"),sQuery(id+"F0.wireOp",EDGE,"E6.24.1"),sQuery(id+"F0.wireOp",EDGE,"E6.24.2"),sQuery(id+"F0.wireOp",EDGE,"E6.25.0"),sQuery(id+"F0.wireOp",EDGE,"E6.25.1"),sQuery(id+"F0.wireOp",EDGE,"E6.25.2"),sQuery(id+"F0.wireOp",EDGE,"E6.26.0"),sQuery(id+"F0.wireOp",EDGE,"E6.26.1"),sQuery(id+"F0.wireOp",EDGE,"E6.26.2"),sQuery(id+"F0.wireOp",EDGE,"E6.27.0"),sQuery(id+"F0.wireOp",EDGE,"E6.27.1"),sQuery(id+"F0.wireOp",EDGE,"E6.27.2"),sQuery(id+"F0.wireOp",EDGE,"E6.28.0"),sQuery(id+"F0.wireOp",EDGE,"E6.28.1"),sQuery(id+"F0.wireOp",EDGE,"E6.28.2"),sQuery(id+"F0.wireOp",EDGE,"E6.29.0"),sQuery(id+"F0.wireOp",EDGE,"E6.29.1"),sQuery(id+"F0.wireOp",EDGE,"E6.29.2"),sQuery(id+"F0.wireOp",EDGE,"E6.30.0"),sQuery(id+"F0.wireOp",EDGE,"E6.30.1"),sQuery(id+"F0.wireOp",EDGE,"E6.30.2"),sQuery(id+"F0.wireOp",EDGE,"E6.31.0"),sQuery(id+"F0.wireOp",EDGE,"E6.31.1"),sQuery(id+"F0.wireOp",EDGE,"E6.31.2"),sQuery(id+"F0.wireOp",EDGE,"E6.32.0"),sQuery(id+"F0.wireOp",EDGE,"E6.32.1"),sQuery(id+"F0.wireOp",EDGE,"E6.32.2"),sQuery(id+"F0.wireOp",EDGE,"E6.33.0"),sQuery(id+"F0.wireOp",EDGE,"E6.33.1"),sQuery(id+"F0.wireOp",EDGE,"E6.33.2"),sQuery(id+"F0.wireOp",EDGE,"E6.34.0"),sQuery(id+"F0.wireOp",EDGE,"E6.34.1"),sQuery(id+"F0.wireOp",EDGE,"E6.34.2"),sQuery(id+"F0.wireOp",EDGE,"E7.trimOffspring"),sQuery(id+"F0.wireOp",EDGE,"E8.trimOffspring"),sQuery(id+"F0.wireOp",EDGE,"E9.trimOffspring"),sQuery(id+"F0.wireOp",EDGE,"E10.trimOffspring"),sQuery(id+"F0.wireOp",EDGE,"E11.trimOffspring"),sQuery(id+"F0.wireOp",EDGE,"E12.trimOffspring"),sQuery(id+"F0.wireOp",EDGE,"E13.trimOffspring"),sQuery(id+"F0.wireOp",EDGE,"E14.trimOffspring"),sQuery(id+"F0.wireOp",EDGE,"E15.trimOffspring"),sQuery(id+"F0.wireOp",EDGE,"E16.trimOffspring"),sQuery(id+"F0.wireOp",EDGE,"E17.trimOffspring"),sQuery(id+"F0.wireOp",EDGE,"E18.trimOffspring"),sQuery(id+"F0.wireOp",EDGE,"E19.trimOffspring"),sQuery(id+"F0.wireOp",EDGE,"E20.trimOffspring"),sQuery(id+"F0.wireOp",EDGE,"E21.trimOffspring"),sQuery(id+"F0.wireOp",EDGE,"E22.trimOffspring"),sQuery(id+"F0.wireOp",EDGE,"E23.trimOffspring"),sQuery(id+"F0.wireOp",EDGE,"E24.trimOffspring"),sQuery(id+"F0.wireOp",EDGE,"E25.trimOffspring"),sQuery(id+"F0.wireOp",EDGE,"E26.trimOffspring"),sQuery(id+"F0.wireOp",EDGE,"E27.trimOffspring"),sQuery(id+"F0.wireOp",EDGE,"E28.trimOffspring"),sQuery(id+"F0.wireOp",EDGE,"E29.trimOffspring"),sQuery(id+"F0.wireOp",EDGE,"E30.trimOffspring"),sQuery(id+"F0.wireOp",EDGE,"E31.trimOffspring"),sQuery(id+"F0.wireOp",EDGE,"E32.trimOffspring"),sQuery(id+"F0.wireOp",EDGE,"E33.trimOffspring"),sQuery(id+"F0.wireOp",EDGE,"E34.trimOffspring"),sQuery(id+"F0.wireOp",EDGE,"E35.trimOffspring"),sQuery(id+"F0.wireOp",EDGE,"E36.trimOffspring"),sQuery(id+"F0.wireOp",EDGE,"E37.trimOffspring"),sQuery(id+"F0.wireOp",EDGE,"E38.trimOffspring"),sQuery(id+"F0.wireOp",EDGE,"E39.trimOffspring"),sQuery(id+"F0.wireOp",EDGE,"E40.trimOffspring")])],"isStart":true});
            extrude(context, id + "F5", {"entities" : qUnion([Q0, Q1, Q2]), "operationType" : NewBodyOperationType.REMOVE, "oppositeDirection" : true, "depth" : 1 * mm, "hasDraft" : true, "draftAngle" : 3 * degree, "draftPullDirection" : true});
        }
    });
